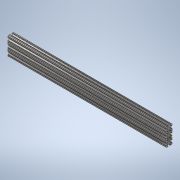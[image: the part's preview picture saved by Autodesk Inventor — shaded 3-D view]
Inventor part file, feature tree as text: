
AUTODESK INVENTOR PART (.ipt)
format: ipt  version: 2020 (Build 240168000, 168)  size: 388,096 bytes
history: native  units: in
note: dims shown in document units (in); Inventor stores cm internally (conversion verified against a paired STEP export)
features: sketch x2, extrude x1
ambient origin geometry x8: Origin, YZ Plane, XZ Plane, XY Plane, X Axis, Y Axis, Z Axis, Center Point
bodies: Solid1 (feature_tree)
feature tree (3):
  extrude  "Extrusion1"  [1 undecoded]
  sketch  "Sketch2"
  sketch  "Sketch1"  dims[d0=26.0in d1=0.0in]
note: 1 required parameter value undecoded (feature->parameter linkage not recoverable at this tier; creation-order binding heuristic only, values carry confidence <= 0.55)
